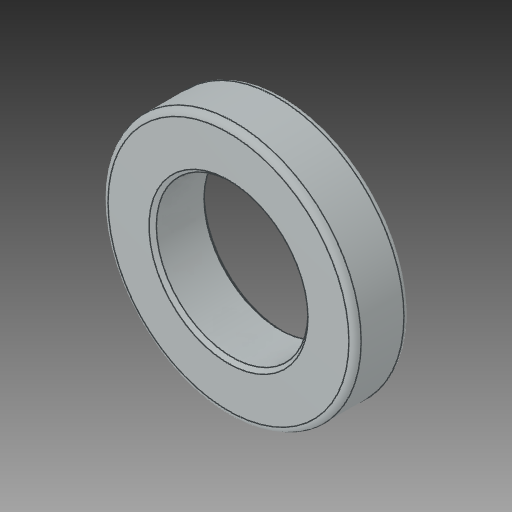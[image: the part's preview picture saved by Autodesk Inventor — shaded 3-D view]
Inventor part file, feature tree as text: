
AUTODESK INVENTOR PART (.ipt)
format: ipt  version: 2018 (Build 220112000, 112)  size: 137,728 bytes
history: native  units: mm
features: other x1, chamfer x1
ambient origin geometry x8: Origin, YZ Plane, XZ Plane, XY Plane, X Axis, Y Axis, Z Axis, Center Point
bodies: Body1 (feature_tree)
feature tree (2):
  other  "ソリッド1"
  chamfer  "Chamfer1"  [1 undecoded]
note: 1 required parameter value undecoded (feature->parameter linkage not recoverable at this tier; creation-order binding heuristic only, values carry confidence <= 0.55)
